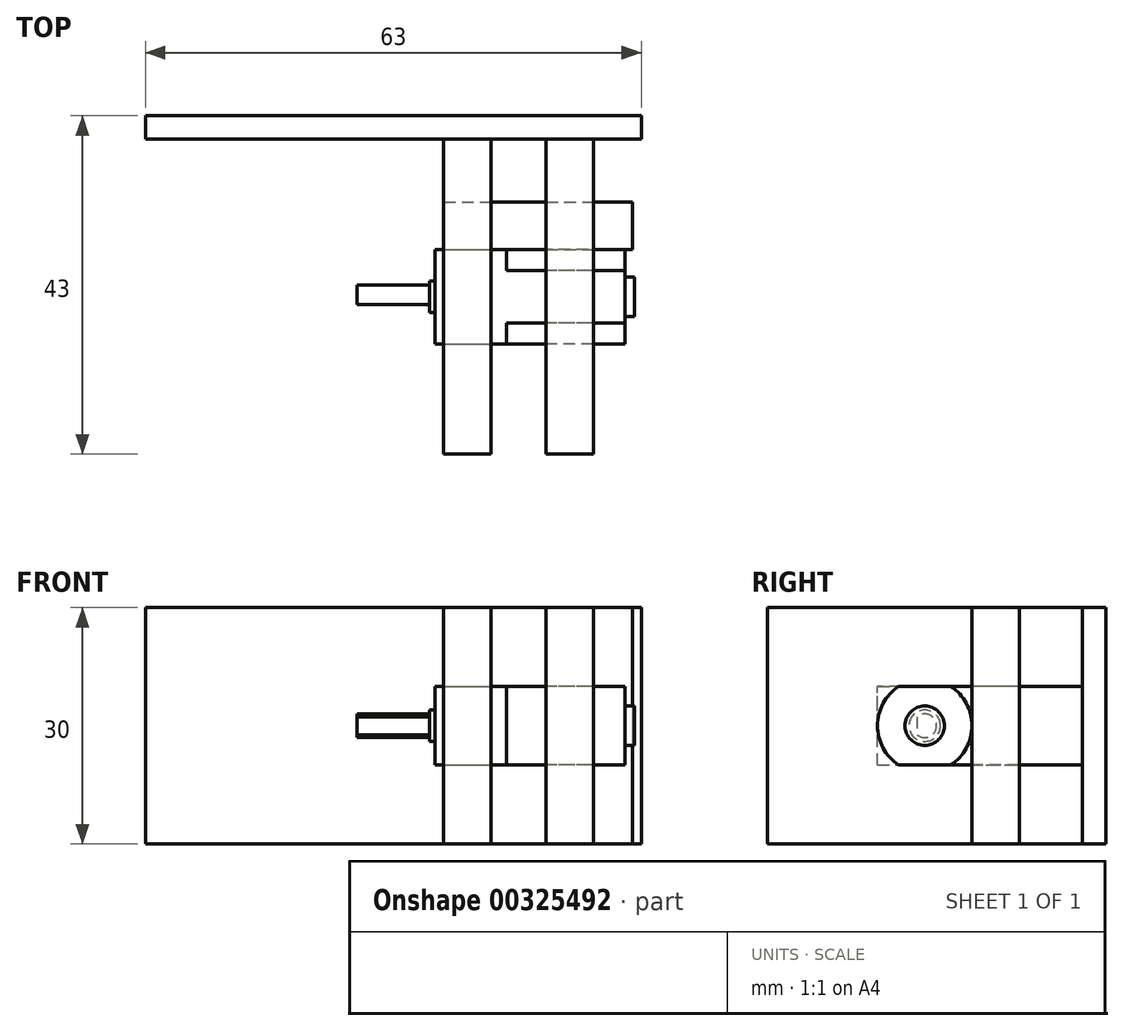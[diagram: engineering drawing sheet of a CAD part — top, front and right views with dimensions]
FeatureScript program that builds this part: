
annotation { "Feature Type Name" : "Feature", "Feature Type Description" : "" }
export const myFeature = defineFeature(function(context is Context, id is Id, definition is map)
    precondition{}
    {
        {
            var Q0;
            Q0=qCreatedBy(makeId("Right.planeOp"),FACE);
            var sketch = newSketch(context, id + "F0", { "sketchPlane" : qUnion([Q0])});
            skLineSegment(sketch, "E0.bottom", {"start": v(3.32, -5) * mm, "end": v(-3.32, -5) * mm});
            skLineSegment(sketch, "E0.top", {"start": v(3.32, 5) * mm, "end": v(-3.32, 5) * mm});
            skLineSegment(sketch, "E0.left", {"start": v(3.32, -5) * mm, "end": v(3.32, 5) * mm, "construction": true});
            skLineSegment(sketch, "E0.right", {"start": v(-3.32, -5) * mm, "end": v(-3.32, 5) * mm, "construction": true});
            skPoint(sketch, "E0.middle", {"position": v(0, 0) * mm});
            skLineSegment(sketch, "E1", {"start": v(0, 5) * mm, "end": v(0, -5) * mm, "construction": true});
            skArc(sketch, "E2", {"start": v(-3.32, 5) * mm, "mid": v(-6, 0) * mm, "end": v(-3.32, -5) * mm});
            skArc(sketch, "E3.trimOffspring", {"start": v(3.32, -5) * mm, "mid": v(6, 0) * mm, "end": v(3.32, 5) * mm});
            skSolve(sketch);
        }
        {
            var Q0;
            Q0 = qSketchRegion(id + "F0", true);
            extrude(context, id + "F1", {"entities" : qUnion([Q0]), "depth" : 15 * mm});
        }
        {
            var Q0;
            Q0=makeQuery(id+"F1.opExtrude","CAP_FACE",FACE,{"disambiguationData":[OSD([sQuery(id+"F0.wireOp",EDGE,"E0.bottom"),sQuery(id+"F0.wireOp",EDGE,"E0.top"),sQuery(id+"F0.wireOp",EDGE,"E2"),sQuery(id+"F0.wireOp",EDGE,"E3.trimOffspring")])],"isStart":false});
            var sketch = newSketch(context, id + "F2", { "sketchPlane" : qUnion([Q0])});
            skCircle(sketch, "E4", {"center": v(0, 0) * mm, "radius": 2.5 * mm});
            skSolve(sketch);
        }
        {
            var Q0;
            Q0 = qSketchRegion(id + "F2", true);
            extrude(context, id + "F3", {"entities" : qUnion([Q0]), "operationType" : NewBodyOperationType.ADD, "depth" : 1.2 * mm});
        }
        {
            var Q0;
            Q0=makeQuery(id+"F1.opExtrude","CAP_FACE",FACE,{"disambiguationData":[OSD([sQuery(id+"F0.wireOp",EDGE,"E0.bottom"),sQuery(id+"F0.wireOp",EDGE,"E0.top"),sQuery(id+"F0.wireOp",EDGE,"E2"),sQuery(id+"F0.wireOp",EDGE,"E3.trimOffspring")])],"isStart":true});
            var sketch = newSketch(context, id + "F4", { "sketchPlane" : qUnion([Q0])});
            skLineSegment(sketch, "E5.bottom", {"start": v(6, -5) * mm, "end": v(-6, -5) * mm});
            skLineSegment(sketch, "E5.top", {"start": v(6, 5) * mm, "end": v(-6, 5) * mm});
            skLineSegment(sketch, "E5.left", {"start": v(6, -5) * mm, "end": v(6, 5) * mm});
            skLineSegment(sketch, "E5.right", {"start": v(-6, -5) * mm, "end": v(-6, 5) * mm});
            skPoint(sketch, "E5.middle", {"position": v(0, 0) * mm});
            skSolve(sketch);
        }
        {
            var Q0;
            Q0 = qSketchRegion(id + "F4", true);
            extrude(context, id + "F5", {"entities" : qUnion([Q0]), "operationType" : NewBodyOperationType.ADD, "depth" : 9.1 * mm});
        }
        {
            var Q0;
            Q0=makeQuery(id+"F5.opExtrude","CAP_FACE",FACE,{"disambiguationData":[OSD([sQuery(id+"F4.wireOp",EDGE,"E5.bottom"),sQuery(id+"F4.wireOp",EDGE,"E5.top"),sQuery(id+"F4.wireOp",EDGE,"E5.left"),sQuery(id+"F4.wireOp",EDGE,"E5.right")])],"isStart":false});
            var sketch = newSketch(context, id + "F6", { "sketchPlane" : qUnion([Q0])});
            skCircle(sketch, "E6", {"center": v(0, 0) * mm, "radius": 2 * mm});
            skSolve(sketch);
        }
        {
            var Q0;
            Q0 = qSketchRegion(id + "F6", true);
            extrude(context, id + "F7", {"entities" : qUnion([Q0]), "operationType" : NewBodyOperationType.ADD, "depth" : 0.7 * mm});
        }
        {
            var Q0;
            Q0=makeQuery(id+"F7.opExtrude","CAP_FACE",FACE,{"disambiguationData":[OSD([sQuery(id+"F6.wireOp",EDGE,"E6")])],"isStart":false});
            var sketch = newSketch(context, id + "F8", { "sketchPlane" : qUnion([Q0])});
            skArc(sketch, "E7", {"start": v(0.97, 1.14) * mm, "mid": v(-1.5, 0) * mm, "end": v(0.97, -1.14) * mm});
            skLineSegment(sketch, "E8", {"start": v(0.97, 1.14) * mm, "end": v(0.97, -1.14) * mm});
            skSolve(sketch);
        }
        {
            var Q0;
            Q0 = qSketchRegion(id + "F8", true);
            extrude(context, id + "F9", {"entities" : qUnion([Q0]), "operationType" : NewBodyOperationType.ADD, "depth" : 9.2 * mm});
        }
        {
            var Q0;
            Q0=qCreatedBy(makeId("Right.planeOp"),FACE);
            cPlane(context, id + "F10", {"entities" : qUnion([Q0]), "cplaneType" : CPlaneType.OFFSET, "offset" : 5 * mm, "width" : 150 * mm, "height" : 150 * mm});
        }
        {
            var Q0;
            Q0=qCreatedBy(id+"F10.planeOp",FACE);
            var sketch = newSketch(context, id + "F11", { "sketchPlane" : qUnion([Q0])});
            skArc(sketch, "E9.0.0", {"start": v(3.32, -5) * mm, "mid": v(6, 0) * mm, "end": v(3.32, 5) * mm, "construction": true});
            skLineSegment(sketch, "E9.0.1", {"start": v(3.32, 5) * mm, "end": v(-3.32, 5) * mm});
            skArc(sketch, "E9.0.2", {"start": v(-3.32, 5) * mm, "mid": v(-6, 0) * mm, "end": v(-3.32, -5) * mm});
            skLineSegment(sketch, "E9.0.3", {"start": v(-3.32, -5) * mm, "end": v(3.32, -5) * mm});
            skLineSegment(sketch, "E10", {"start": v(-3.32, 5) * mm, "end": v(20, 5) * mm});
            skLineSegment(sketch, "E11", {"start": v(-3.32, -5) * mm, "end": v(20, -5) * mm});
            skLineSegment(sketch, "E12.bottom", {"start": v(-20, -15) * mm, "end": v(20, -15) * mm});
            skLineSegment(sketch, "E12.top", {"start": v(-20, 15) * mm, "end": v(20, 15) * mm});
            skLineSegment(sketch, "E12.left", {"start": v(-20, -15) * mm, "end": v(-20, 15) * mm});
            skLineSegment(sketch, "E12.right", {"start": v(20, -15) * mm, "end": v(20, -5) * mm});
            skCircle(sketch, "E13", {"center": v(0, 0) * mm, "radius": 10 * mm, "construction": true});
            skLineSegment(sketch, "E14.trimOffspring", {"start": v(20, 5) * mm, "end": v(20, 15) * mm});
            skSolve(sketch);
        }
        {
            var Q0;
            Q0 = qSketchRegion(id + "F11", true);
            extrude(context, id + "F12", {"entities" : qUnion([Q0]), "depth" : 6 * mm});
        }
        {
            var Q0;
            Q0=makeQuery(id+"F12.opExtrude","SWEPT_FACE",FACE,{"disambiguationData":[OSD([sQuery(id+"F11.wireOp",EDGE,"E14.trimOffspring")])]});
            var sketch = newSketch(context, id + "F13", { "sketchPlane" : qUnion([Q0])});
            skLineSegment(sketch, "E15.0.0", {"start": v(9.8, 1.5) * mm, "end": v(9.8, -1.5) * mm, "construction": true});
            skLineSegment(sketch, "E15.0.2", {"start": v(19, -1.5) * mm, "end": v(19, 1.5) * mm, "construction": true});
            skLineSegment(sketch, "E16", {"start": v(19, 0) * mm, "end": v(9.8, 0) * mm, "construction": true});
            skPoint(sketch, "E17", {"position": v(14.4, 0) * mm});
            skLineSegment(sketch, "E18.bottom", {"start": v(-17.1, -15) * mm, "end": v(45.9, -15) * mm});
            skLineSegment(sketch, "E18.top", {"start": v(-17.1, 15) * mm, "end": v(45.9, 15) * mm});
            skLineSegment(sketch, "E18.left", {"start": v(-17.1, -15) * mm, "end": v(-17.1, 15) * mm});
            skLineSegment(sketch, "E18.right", {"start": v(45.9, -15) * mm, "end": v(45.9, 15) * mm});
            skSolve(sketch);
        }
        {
            var Q0;
            Q0 = qSketchRegion(id + "F13", true);
            extrude(context, id + "F14", {"entities" : qUnion([Q0]), "depth" : 3 * mm});
        }
        {
            var Q0;
            Q0=qCreatedBy(makeId("Right.planeOp"),FACE);
            cPlane(context, id + "F15", {"entities" : qUnion([Q0]), "cplaneType" : CPlaneType.OFFSET, "offset" : 2 * mm, "oppositeDirection" : true, "width" : 150 * mm, "height" : 150 * mm});
        }
        {
            var Q0;
            Q0=qCreatedBy(id+"F15.planeOp",FACE);
            var sketch = newSketch(context, id + "F16", { "sketchPlane" : qUnion([Q0])});
            skLineSegment(sketch, "E19.0.0", {"start": v(6, -5) * mm, "end": v(-6, -5) * mm});
            skLineSegment(sketch, "E19.0.1", {"start": v(-6, -5) * mm, "end": v(-6, 5) * mm});
            skLineSegment(sketch, "E19.0.2", {"start": v(-6, 5) * mm, "end": v(6, 5) * mm});
            skLineSegment(sketch, "E19.0.3", {"start": v(6, 5) * mm, "end": v(6, -5) * mm, "construction": true});
            skLineSegment(sketch, "E20.0.0", {"start": v(-20, -15) * mm, "end": v(-20, 15) * mm});
            skLineSegment(sketch, "E20.0.1", {"start": v(-20, 15) * mm, "end": v(20, 15) * mm});
            skLineSegment(sketch, "E20.0.2", {"start": v(20, 15) * mm, "end": v(20, 5) * mm});
            skLineSegment(sketch, "E20.0.3", {"start": v(20, 5) * mm, "end": v(-3.32, 5) * mm});
            skArc(sketch, "E20.0.4", {"start": v(-3.32, 5) * mm, "mid": v(-6, 0) * mm, "end": v(-3.32, -5) * mm, "construction": true});
            skLineSegment(sketch, "E20.0.5", {"start": v(-3.32, -5) * mm, "end": v(20, -5) * mm});
            skLineSegment(sketch, "E20.0.6", {"start": v(20, -5) * mm, "end": v(20, -15) * mm});
            skLineSegment(sketch, "E20.0.7", {"start": v(20, -15) * mm, "end": v(-20, -15) * mm});
            skSolve(sketch);
        }
        {
            var Q0;
            Q0 = qSketchRegion(id + "F16", true);
            extrude(context, id + "F17", {"entities" : qUnion([Q0]), "oppositeDirection" : true, "depth" : 6 * mm});
        }
        {
            var Q0;
            Q0=makeQuery(id+"F5.opExtrude","SWEPT_FACE",FACE,{"disambiguationData":[OSD([sQuery(id+"F4.wireOp",EDGE,"E5.right")])]});
            var sketch = newSketch(context, id + "F18", { "sketchPlane" : qUnion([Q0])});
            skLineSegment(sketch, "E21.0", {"start": v(8, 5) * mm, "end": v(2, 5) * mm, "construction": true});
            skLineSegment(sketch, "E22.0", {"start": v(8, -5) * mm, "end": v(2, -5) * mm, "construction": true});
            skLineSegment(sketch, "E23.0", {"start": v(-11, 5) * mm, "end": v(-11, 15) * mm, "construction": true});
            skLineSegment(sketch, "E24.0", {"start": v(-11, -15) * mm, "end": v(-11, -5) * mm, "construction": true});
            skLineSegment(sketch, "E25", {"start": v(8, 5) * mm, "end": v(-11, 5) * mm});
            skLineSegment(sketch, "E26", {"start": v(-11, 15) * mm, "end": v(-16, 15) * mm});
            skLineSegment(sketch, "E27", {"start": v(-16, 15) * mm, "end": v(-16, -15) * mm});
            skLineSegment(sketch, "E28", {"start": v(-16, -15) * mm, "end": v(-11, -15) * mm});
            skLineSegment(sketch, "E29", {"start": v(-11, -5) * mm, "end": v(8, -5) * mm});
            skLineSegment(sketch, "E30", {"start": v(8, 5) * mm, "end": v(8, -5) * mm});
            skLineSegment(sketch, "E31", {"start": v(-11, 15) * mm, "end": v(-11, 5) * mm});
            skLineSegment(sketch, "E32", {"start": v(-11, -5) * mm, "end": v(-11, -15) * mm});
            skSolve(sketch);
        }
        {
            var Q0;
            Q0 = qSketchRegion(id + "F18", true);
            extrude(context, id + "F19", {"entities" : qUnion([Q0]), "depth" : 6 * mm});
        }
    });
